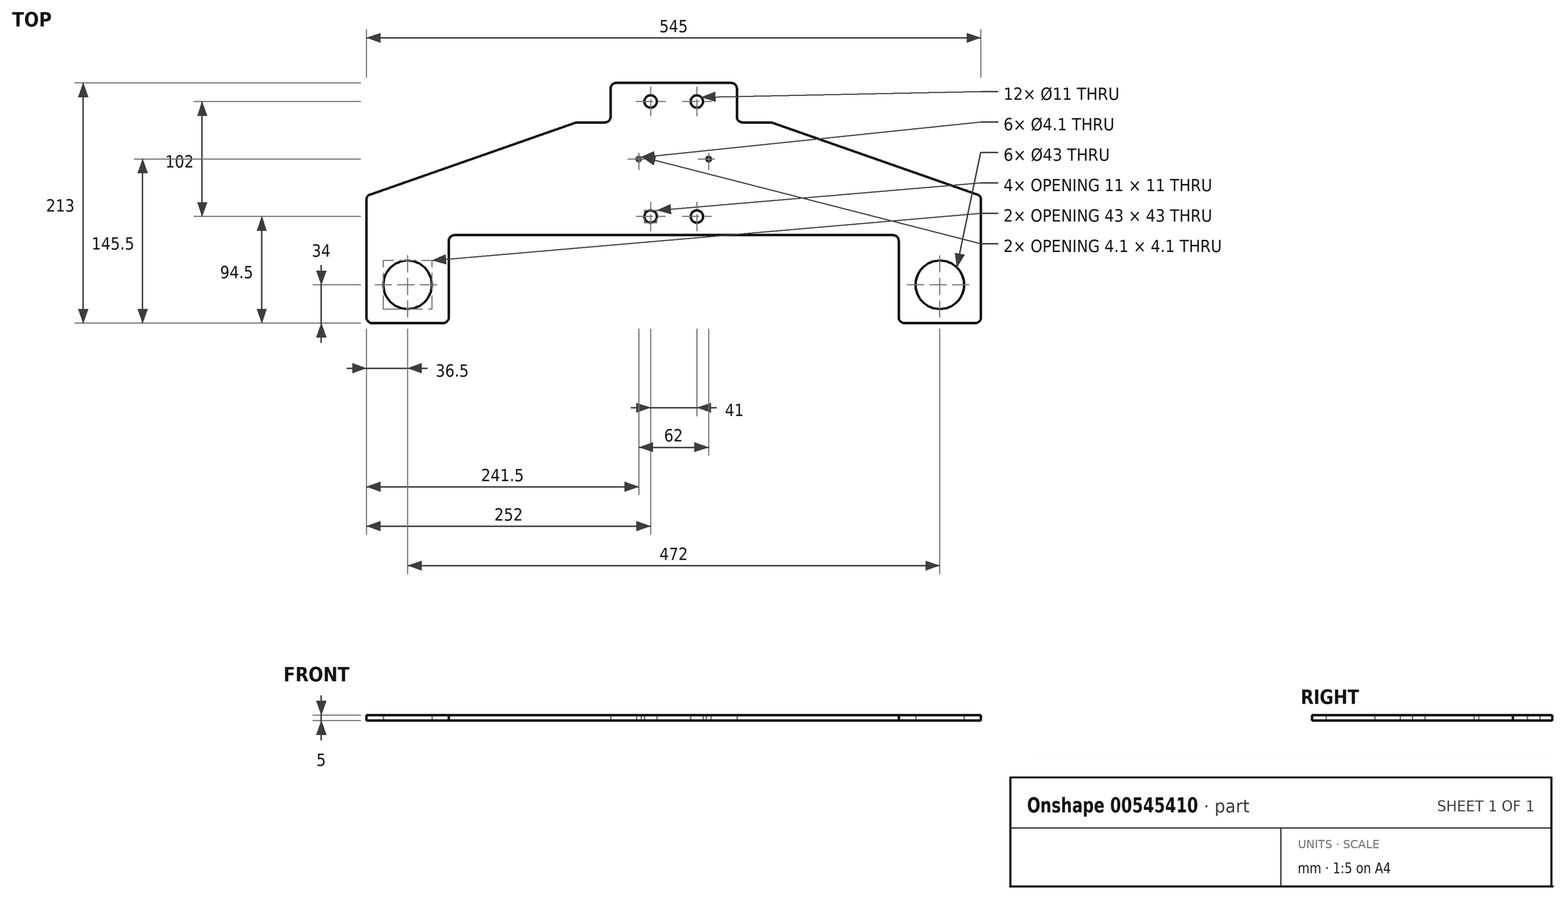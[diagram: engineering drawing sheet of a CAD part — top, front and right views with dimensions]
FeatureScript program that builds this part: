
annotation { "Feature Type Name" : "Feature", "Feature Type Description" : "" }
export const myFeature = defineFeature(function(context is Context, id is Id, definition is map)
    precondition{}
    {
        {
            var Q0;
            Q0=qCreatedBy(makeId("Top.planeOp"),FACE);
            var sketch = newSketch(context, id + "F0", { "sketchPlane" : qUnion([Q0])});
            skLineSegment(sketch, "E0", {"start": v(-86, 50) * mm, "end": v(86, 50) * mm});
            skLineSegment(sketch, "E1", {"start": v(-272.5, -50) * mm, "end": v(272.5, -50) * mm});
            skLineSegment(sketch, "E2", {"start": v(-272.5, -50) * mm, "end": v(-272.5, -128) * mm});
            skLineSegment(sketch, "E3", {"start": v(272.5, -50) * mm, "end": v(272.5, -128) * mm});
            skLineSegment(sketch, "E4", {"start": v(272.5, -128) * mm, "end": v(199.5, -128) * mm});
            skLineSegment(sketch, "E5", {"start": v(199.5, -128) * mm, "end": v(199.5, -50) * mm});
            skLineSegment(sketch, "E6", {"start": v(-272.5, -128) * mm, "end": v(-199.5, -128) * mm});
            skLineSegment(sketch, "E7", {"start": v(-199.5, -128) * mm, "end": v(-199.5, -50) * mm});
            skLineSegment(sketch, "E8", {"start": v(-272.5, -50) * mm, "end": v(-272.5, -15) * mm});
            skLineSegment(sketch, "E9", {"start": v(-272.5, -15) * mm, "end": v(-86, 50) * mm});
            skLineSegment(sketch, "E10", {"start": v(272.5, -50) * mm, "end": v(272.5, -15) * mm});
            skLineSegment(sketch, "E11", {"start": v(86, 50) * mm, "end": v(272.5, -15) * mm});
            skLineSegment(sketch, "E12", {"start": v(56, 50) * mm, "end": v(56, 85) * mm});
            skLineSegment(sketch, "E13", {"start": v(56, 85) * mm, "end": v(-56, 85) * mm});
            skLineSegment(sketch, "E14", {"start": v(-56, 85) * mm, "end": v(-56, 50) * mm});
            skSolve(sketch);
        }
        {
            var Q0;
            Q0=makeQuery(id+"F0.imprint","IMPRINT",FACE,{"disambiguationData":[TD([[makeQuery(id+"F0.imprint","IMPRINT",EDGE,{"derivedFrom":sQuery(id+"F0.wireOp",EDGE,"E0")}),-1.0]])]});
            var Q1;
            {var subQ0=sQuery(id+"F0.wireOp",EDGE,"E2");Q1=makeQuery(id+"F0.imprint","IMPRINT",FACE,{"disambiguationData":[TD([[makeQuery(id+"F0.imprint","IMPRINT",EDGE,{"derivedFrom":subQ0}),1.0]])]});}
            var Q2;
            {var subQ0=sQuery(id+"F0.wireOp",EDGE,"E3");Q2=makeQuery(id+"F0.imprint","IMPRINT",FACE,{"disambiguationData":[TD([[makeQuery(id+"F0.imprint","IMPRINT",EDGE,{"derivedFrom":subQ0}),-1.0]])]});}
            var Q3;
            {var subQ0=sQuery(id+"F0.wireOp",EDGE,"E12");Q3=makeQuery(id+"F0.imprint","IMPRINT",FACE,{"disambiguationData":[TD([[makeQuery(id+"F0.imprint","IMPRINT",EDGE,{"derivedFrom":subQ0}),1.0]])]});}
            extrude(context, id + "F1", {"entities" : qUnion([Q0, Q1, Q2, Q3]), "depth" : 5 * mm});
        }
        {
            var Q0;
            Q0=makeQuery(id+"F1.opExtrude","SWEPT_EDGE",EDGE,{"disambiguationData":[OSD([sQuery(id+"F0.wireOp",EDGE,"E2"),sQuery(id+"F0.wireOp",EDGE,"E6")])]});
            var Q1;
            Q1=makeQuery(id+"F1.opExtrude","SWEPT_EDGE",EDGE,{"disambiguationData":[OSD([sQuery(id+"F0.wireOp",EDGE,"E6"),sQuery(id+"F0.wireOp",EDGE,"E7")])]});
            var Q2;
            Q2=makeQuery(id+"F1.opExtrude","SWEPT_EDGE",EDGE,{"disambiguationData":[OSD([sQuery(id+"F0.wireOp",EDGE,"E4"),sQuery(id+"F0.wireOp",EDGE,"E5")])]});
            var Q3;
            Q3=makeQuery(id+"F1.opExtrude","SWEPT_EDGE",EDGE,{"disambiguationData":[OSD([sQuery(id+"F0.wireOp",EDGE,"E3"),sQuery(id+"F0.wireOp",EDGE,"E4")])]});
            var Q4;
            Q4=makeQuery(id+"F1.opExtrude","SWEPT_EDGE",EDGE,{"disambiguationData":[OSD([sQuery(id+"F0.wireOp",EDGE,"E10"),sQuery(id+"F0.wireOp",EDGE,"E11")])]});
            var Q5;
            Q5=makeQuery(id+"F1.opExtrude","SWEPT_EDGE",EDGE,{"disambiguationData":[OSD([sQuery(id+"F0.wireOp",EDGE,"E8"),sQuery(id+"F0.wireOp",EDGE,"E9")])]});
            var Q6;
            Q6=makeQuery(id+"F1.opExtrude","SWEPT_EDGE",EDGE,{"disambiguationData":[OSD([sQuery(id+"F0.wireOp",EDGE,"E1"),sQuery(id+"F0.wireOp",EDGE,"E7")])]});
            var Q7;
            Q7=makeQuery(id+"F1.opExtrude","SWEPT_EDGE",EDGE,{"disambiguationData":[OSD([sQuery(id+"F0.wireOp",EDGE,"E1"),sQuery(id+"F0.wireOp",EDGE,"E5")])]});
            var Q8;
            Q8=makeQuery(id+"F1.opExtrude","SWEPT_EDGE",EDGE,{"disambiguationData":[OSD([sQuery(id+"F0.wireOp",EDGE,"E0"),sQuery(id+"F0.wireOp",EDGE,"E14")])]});
            var Q9;
            Q9=makeQuery(id+"F1.opExtrude","SWEPT_EDGE",EDGE,{"disambiguationData":[OSD([sQuery(id+"F0.wireOp",EDGE,"E13"),sQuery(id+"F0.wireOp",EDGE,"E14")])]});
            var Q10;
            Q10=makeQuery(id+"F1.opExtrude","SWEPT_EDGE",EDGE,{"disambiguationData":[OSD([sQuery(id+"F0.wireOp",EDGE,"E12"),sQuery(id+"F0.wireOp",EDGE,"E13")])]});
            var Q11;
            Q11=makeQuery(id+"F1.opExtrude","SWEPT_EDGE",EDGE,{"disambiguationData":[OSD([sQuery(id+"F0.wireOp",EDGE,"E0"),sQuery(id+"F0.wireOp",EDGE,"E12")])]});
            fillet(context, id + "F2", {"entities" : qUnion([Q0, Q1, Q2, Q3, Q4, Q5, Q6, Q7, Q8, Q9, Q10, Q11]), "radius" : 5 * mm, "tangentPropagation" : true, "allowEdgeOverflow" : false});
        }
        {
            var Q0;
            Q0=makeQuery(id+"F1.opExtrude","SWEPT_EDGE",EDGE,{"disambiguationData":[OSD([sQuery(id+"F0.wireOp",EDGE,"E0"),sQuery(id+"F0.wireOp",EDGE,"E11")])]});
            var Q1;
            Q1=makeQuery(id+"F1.opExtrude","SWEPT_EDGE",EDGE,{"disambiguationData":[OSD([sQuery(id+"F0.wireOp",EDGE,"E0"),sQuery(id+"F0.wireOp",EDGE,"E9")])]});
            fillet(context, id + "F3", {"entities" : qUnion([Q0, Q1]), "radius" : 5 * mm, "tangentPropagation" : true, "allowEdgeOverflow" : false});
        }
        {
            var Q0;
            Q0=qCreatedBy(makeId("Top.planeOp"),FACE);
            var sketch = newSketch(context, id + "F4", { "sketchPlane" : qUnion([Q0])});
            skCircle(sketch, "E15", {"center": v(-20.5, 68.5) * mm, "radius": 5.5 * mm});
            skCircle(sketch, "E16", {"center": v(20.5, 68.5) * mm, "radius": 5.5 * mm});
            skCircle(sketch, "E17", {"center": v(-20.5, -33.5) * mm, "radius": 4.83 * mm});
            skCircle(sketch, "E18", {"center": v(20.5, -33.5) * mm, "radius": 5.14 * mm});
            skSolve(sketch);
        }
        {
            var Q0;
            Q0=qCreatedBy(makeId("Top.planeOp"),FACE);
            var sketch = newSketch(context, id + "F5", { "sketchPlane" : qUnion([Q0])});
            skCircle(sketch, "E19", {"center": v(-31, 17.5) * mm, "radius": 4.53 * mm});
            skCircle(sketch, "E20", {"center": v(31, 17.5) * mm, "radius": 4.22 * mm});
            skSolve(sketch);
        }
        {
            var Q0;
            Q0=sQuery(id+"F5.wireOp",VERTEX,"E19.center");
            var Q1;
            Q1=sQuery(id+"F5.wireOp",VERTEX,"E20.center");
            var Q2;
            Q2=makeQuery(id+"F1.opExtrude","SWEPT_BODY",BODY,{"disambiguationData":[OSD([sQuery(id+"F0.wireOp",EDGE,"E0"),sQuery(id+"F0.wireOp",EDGE,"E1"),sQuery(id+"F0.wireOp",EDGE,"E2"),sQuery(id+"F0.wireOp",EDGE,"E3"),sQuery(id+"F0.wireOp",EDGE,"E4"),sQuery(id+"F0.wireOp",EDGE,"E5"),sQuery(id+"F0.wireOp",EDGE,"E6"),sQuery(id+"F0.wireOp",EDGE,"E7"),sQuery(id+"F0.wireOp",EDGE,"E8"),sQuery(id+"F0.wireOp",EDGE,"E9"),sQuery(id+"F0.wireOp",EDGE,"E10"),sQuery(id+"F0.wireOp",EDGE,"E11")])]});
            hole(context, id + "F6", {"style" : HoleStyle.SIMPLE, "endStyle" : HoleEndStyle.THROUGH, "oppositeDirection" : true, "holeDiameter" : 4.1 * mm, "tappedDepth" : 12 * mm, "tapClearance" : 3, "locations" : qUnion([Q0, Q1]), "scope" : qUnion([Q2])});
        }
        {
            var Q0;
            Q0=qCreatedBy(makeId("Top.planeOp"),FACE);
            var sketch = newSketch(context, id + "F7", { "sketchPlane" : qUnion([Q0])});
            skCircle(sketch, "E21", {"center": v(-236, -94) * mm, "radius": 11.57 * mm});
            skCircle(sketch, "E22", {"center": v(236, -94) * mm, "radius": 8.32 * mm});
            skSolve(sketch);
        }
        {
            var Q0;
            Q0=sQuery(id+"F7.wireOp",VERTEX,"E21.center");
            var Q1;
            Q1=sQuery(id+"F7.wireOp",VERTEX,"E22.center");
            var Q2;
            Q2=makeQuery(id+"F1.opExtrude","SWEPT_BODY",BODY,{"disambiguationData":[OSD([sQuery(id+"F0.wireOp",EDGE,"E0"),sQuery(id+"F0.wireOp",EDGE,"E1"),sQuery(id+"F0.wireOp",EDGE,"E2"),sQuery(id+"F0.wireOp",EDGE,"E3"),sQuery(id+"F0.wireOp",EDGE,"E4"),sQuery(id+"F0.wireOp",EDGE,"E5"),sQuery(id+"F0.wireOp",EDGE,"E6"),sQuery(id+"F0.wireOp",EDGE,"E7"),sQuery(id+"F0.wireOp",EDGE,"E8"),sQuery(id+"F0.wireOp",EDGE,"E9"),sQuery(id+"F0.wireOp",EDGE,"E10"),sQuery(id+"F0.wireOp",EDGE,"E11")])]});
            hole(context, id + "F8", {"style" : HoleStyle.SIMPLE, "endStyle" : HoleEndStyle.THROUGH, "oppositeDirection" : true, "holeDiameter" : 43 * mm, "tappedDepth" : 12 * mm, "tapClearance" : 3, "locations" : qUnion([Q0, Q1]), "scope" : qUnion([Q2])});
        }
        {
            var Q0;
            Q0=sQuery(id+"F4.wireOp",VERTEX,"E15.center");
            var Q1;
            Q1=sQuery(id+"F4.wireOp",VERTEX,"E16.center");
            var Q2;
            Q2=sQuery(id+"F4.wireOp",VERTEX,"V0FrDJi0-5RUE-7QYn-pTRS-WBAOulQvoWCY.center");
            var Q3;
            Q3=sQuery(id+"F4.wireOp",VERTEX,"E17.center");
            var Q4;
            Q4=sQuery(id+"F4.wireOp",VERTEX,"E18.center");
            var Q5;
            Q5=makeQuery(id+"F1.opExtrude","SWEPT_BODY",BODY,{"disambiguationData":[OSD([sQuery(id+"F0.wireOp",EDGE,"E0"),sQuery(id+"F0.wireOp",EDGE,"E1"),sQuery(id+"F0.wireOp",EDGE,"E2"),sQuery(id+"F0.wireOp",EDGE,"E3"),sQuery(id+"F0.wireOp",EDGE,"E4"),sQuery(id+"F0.wireOp",EDGE,"E5"),sQuery(id+"F0.wireOp",EDGE,"E6"),sQuery(id+"F0.wireOp",EDGE,"E7"),sQuery(id+"F0.wireOp",EDGE,"E8"),sQuery(id+"F0.wireOp",EDGE,"E9"),sQuery(id+"F0.wireOp",EDGE,"E10"),sQuery(id+"F0.wireOp",EDGE,"E11"),sQuery(id+"F0.wireOp",EDGE,"E12"),sQuery(id+"F0.wireOp",EDGE,"E13"),sQuery(id+"F0.wireOp",EDGE,"E14")])]});
            hole(context, id + "F9", {"style" : HoleStyle.SIMPLE, "endStyle" : HoleEndStyle.THROUGH, "oppositeDirection" : true, "standardTappedOrClearance" : lookupTablePath({ "standard" : "ISO", "fit" : "Normal", "size" : "M10", "type" : "Clearance" }), "standardBlindInLast" : lookupTablePath({ "fit" : "Standard", "standard" : "ISO", "size" : "M10", "type" : "Clearance" }), "holeDiameter" : 11 * mm, "tappedDepth" : 12 * mm, "tapClearance" : 3, "locations" : qUnion([Q0, Q1, Q2, Q3, Q4]), "scope" : qUnion([Q5])});
        }
    });
